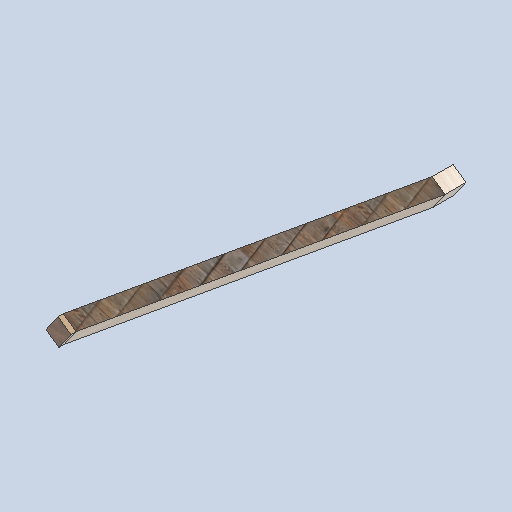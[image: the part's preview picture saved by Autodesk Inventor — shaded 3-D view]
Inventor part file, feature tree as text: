
AUTODESK INVENTOR PART (.ipt)
format: ipt  version: 2024.2 (Build 282272000, 272)  size: 315,392 bytes
history: native  units: mm
features: sketch x4, plane x2, extrude x2, projected_geometry x2, loft x1
ambient origin geometry x8: Origin, YZ Plane, XZ Plane, XY Plane, X Axis, Y Axis, Z Axis, Center Point
bodies: Solid1 (feature_tree)
feature tree (11):
  sketch  "Sketch1"  dims[d0=0.0mm d1=3749.0mm d2=0.0mm d3=90.0deg]
  plane  "Work Plane2"
  loft  "Loft1"
  sketch  "Sketch3"  dims[d8=50.0mm d9=0.0mm]
  sketch  "Sketch4"
  extrude  "Extrusion1"  Depth=200.0mm TaperAngle=0.0deg
  extrude  "Extrusion2"  [1 undecoded]
  plane  "Work Plane1"
  sketch  "Sketch2"  dims[d4=0.0mm d5=90.0deg d6=200.0mm d7=0.0mm]
  projected_geometry  "Projected Loop1"
  projected_geometry  "Projected Loop2"
note: 1 required parameter value undecoded (feature->parameter linkage not recoverable at this tier; creation-order binding heuristic only, values carry confidence <= 0.55)
